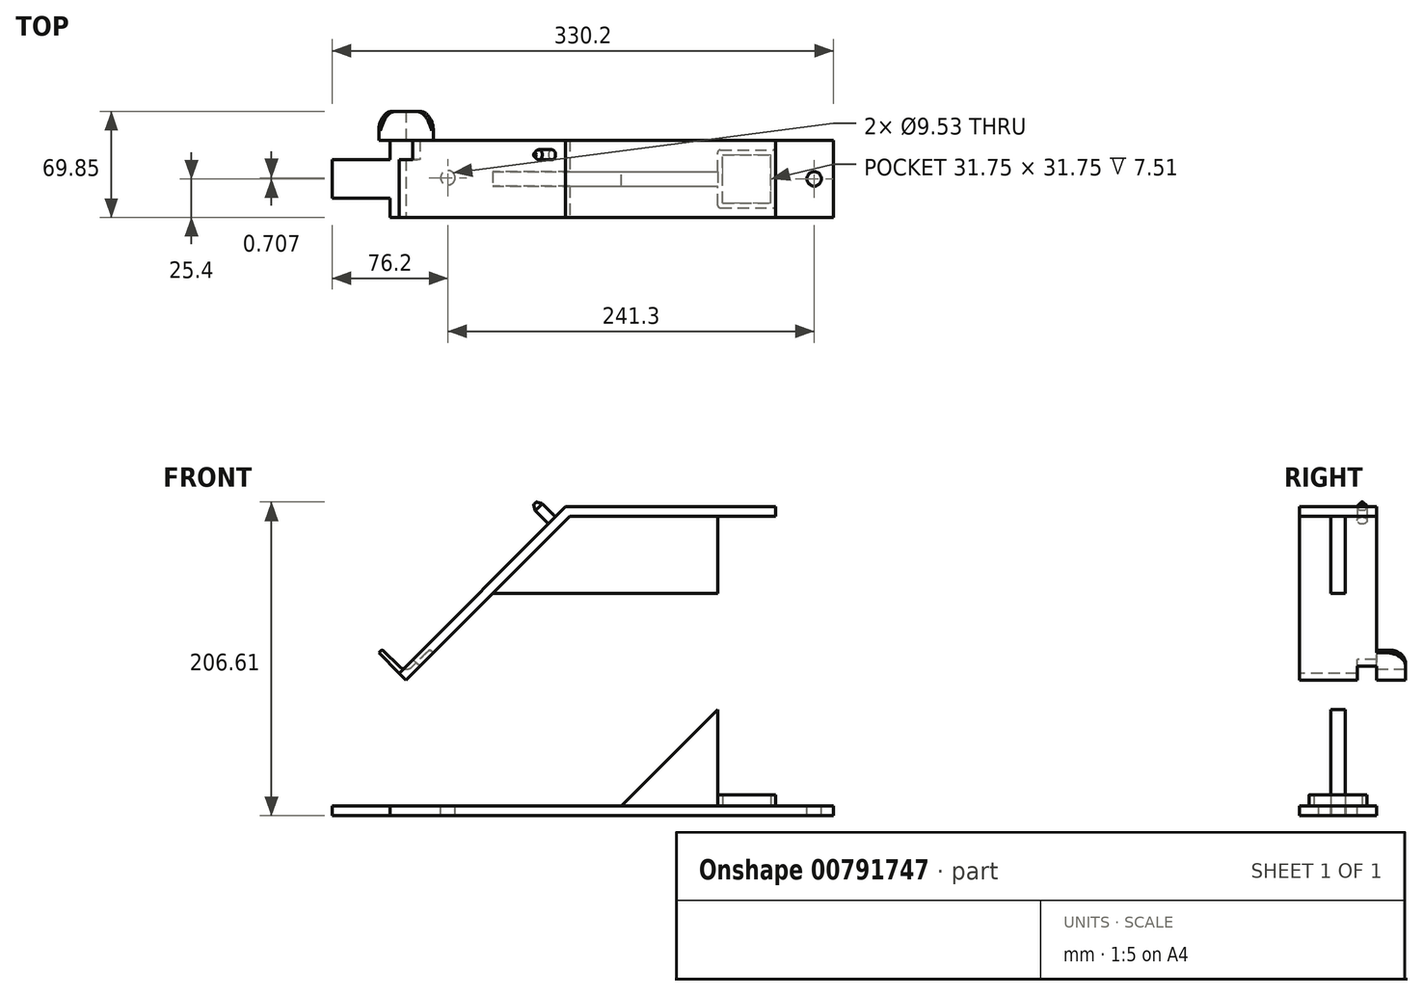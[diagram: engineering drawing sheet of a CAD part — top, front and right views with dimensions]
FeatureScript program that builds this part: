
annotation { "Feature Type Name" : "Feature", "Feature Type Description" : "" }
export const myFeature = defineFeature(function(context is Context, id is Id, definition is map)
    precondition{}
    {
        {
            assignVariable(context, id + "F0", {"name" : "haut", "anyValue" : 8 - 0.49});
        }
        {
            var Q0;
            Q0=qCreatedBy(makeId("Top.planeOp"),FACE);
            var sketch = newSketch(context, id + "F1", { "sketchPlane" : qUnion([Q0])});
            skLineSegment(sketch, "E0.bottom", {"start": v(0, 0) * mm, "end": v(114.3, 0) * mm});
            skLineSegment(sketch, "E0.top", {"start": v(0, 50.8) * mm, "end": v(114.3, 50.8) * mm});
            skLineSegment(sketch, "E0.left", {"start": v(0, 0) * mm, "end": v(0, 50.8) * mm});
            skLineSegment(sketch, "E0.right", {"start": v(114.3, 0) * mm, "end": v(114.3, 50.8) * mm});
            skLineSegment(sketch, "E1.bottom", {"start": v(0, 0) * mm, "end": v(-177.8, 0) * mm});
            skLineSegment(sketch, "E1.top", {"start": v(0, 50.8) * mm, "end": v(-177.8, 50.8) * mm});
            skLineSegment(sketch, "E1.right", {"start": v(-215.9, 12.7) * mm, "end": v(-215.9, 38.1) * mm});
            skLineSegment(sketch, "E2.top", {"start": v(-215.9, 38.1) * mm, "end": v(-177.8, 38.1) * mm});
            skLineSegment(sketch, "E2.right", {"start": v(-177.8, 50.8) * mm, "end": v(-177.8, 38.1) * mm});
            skLineSegment(sketch, "E3.top", {"start": v(-215.9, 12.7) * mm, "end": v(-177.8, 12.7) * mm});
            skLineSegment(sketch, "E3.right", {"start": v(-177.8, 0) * mm, "end": v(-177.8, 12.7) * mm});
            skCircle(sketch, "E4", {"center": v(101.6, 25.4) * mm, "radius": 4.76 * mm});
            skCircle(sketch, "E5", {"center": v(-139.7, 26.1) * mm, "radius": 4.76 * mm});
            skSolve(sketch);
        }
        {
            var Q0;
            Q0=qSketchRegion(id+"F1",true);
            extrude(context, id + "F2", {"entities" : qUnion([Q0]), "oppositeDirection" : true, "depth" : 6.35 * mm, "offsetDistance" : 25.4 * mm});
        }
        {
            var Q0;
            Q0=makeQuery(id+"F2.opExtrude","CAP_FACE",FACE,{"disambiguationData":[OSD([sQuery(id+"F1.wireOp",EDGE,"E0.bottom"),sQuery(id+"F1.wireOp",EDGE,"E0.top"),sQuery(id+"F1.wireOp",EDGE,"E0.left"),sQuery(id+"F1.wireOp",EDGE,"E0.right")])],"isStart":true});
            var sketch = newSketch(context, id + "F3", { "sketchPlane" : qUnion([Q0])});
            skLineSegment(sketch, "E6.bottom", {"start": v(38.1, 6.35) * mm, "end": v(76.2, 6.35) * mm});
            skLineSegment(sketch, "E6.top", {"start": v(38.1, 44.45) * mm, "end": v(76.2, 44.45) * mm});
            skLineSegment(sketch, "E6.left", {"start": v(38.1, 6.35) * mm, "end": v(38.1, 44.45) * mm});
            skLineSegment(sketch, "E6.right", {"start": v(76.2, 6.35) * mm, "end": v(76.2, 44.45) * mm});
            skLineSegment(sketch, "E7.0", {"start": v(41.27, 41.28) * mm, "end": v(73.03, 41.28) * mm});
            skLineSegment(sketch, "E7.1", {"start": v(41.27, 9.52) * mm, "end": v(41.27, 41.28) * mm});
            skLineSegment(sketch, "E7.2", {"start": v(41.27, 9.52) * mm, "end": v(73.03, 9.53) * mm});
            skLineSegment(sketch, "E7.3", {"start": v(73.03, 9.53) * mm, "end": v(73.03, 41.28) * mm});
            skSolve(sketch);
        }
        {
            var Q0;
            Q0=qSketchRegion(id+"F3",true);
            extrude(context, id + "F4", {"entities" : qUnion([Q0]), "operationType" : NewBodyOperationType.ADD, "depth" : (getVariable(context, 'haut')) * mm, "offsetDistance" : 25.4 * mm});
        }
        {
            var Q0;
            Q0=makeQuery(id+"F4.opExtrude","SWEPT_FACE",FACE,{"disambiguationData":[OSD([sQuery(id+"F3.wireOp",EDGE,"E6.bottom")])]});
            var sketch = newSketch(context, id + "F5", { "sketchPlane" : qUnion([Q0])});
            skLineSegment(sketch, "E8", {"start": v(76.2, 190.76) * mm, "end": v(-59.52, 190.76) * mm});
            skLineSegment(sketch, "E9", {"start": v(-59.52, 190.76) * mm, "end": v(-167.28, 83) * mm});
            skLineSegment(sketch, "E10.0", {"start": v(76.2, 197.11) * mm, "end": v(-62.15, 197.11) * mm});
            skLineSegment(sketch, "E11.0", {"start": v(-62.15, 197.11) * mm, "end": v(-171.77, 87.5) * mm});
            skLineSegment(sketch, "E12", {"start": v(-167.28, 83) * mm, "end": v(-171.77, 87.5) * mm});
            skLineSegment(sketch, "E13", {"start": v(76.2, 190.76) * mm, "end": v(76.2, 197.11) * mm});
            skSolve(sketch);
        }
        {
            var Q0;
            Q0=qSketchRegion(id+"F5",true);
            extrude(context, id + "F6", {"entities" : qUnion([Q0]), "operationType" : NewBodyOperationType.ADD, "oppositeDirection" : true, "depth" : 44.45 * mm, "offsetDistance" : 25.4 * mm, "hasSecondDirection" : true, "secondDirectionOppositeDirection" : false, "secondDirectionDepth" : 6.35 * mm});
        }
        {
            var Q0;
            Q0=makeQuery(id+"F6.opExtrude","SWEPT_FACE",FACE,{"disambiguationData":[OSD([sQuery(id+"F5.wireOp",EDGE,"E11.0")])]});
            var sketch = newSketch(context, id + "F7", { "sketchPlane" : qUnion([Q0])});
            skCircle(sketch, "E14", {"center": v(-41.28, 82.74) * mm, "radius": 3.3 * mm});
            skLineSegment(sketch, "E15.direction1", {"start": v(-41.28, 82.74) * mm, "end": v(-15.88, 82.74) * mm, "construction": true});
            skLineSegment(sketch, "E15.direction2", {"start": v(-41.28, 82.74) * mm, "end": v(-41.28, -44.26) * mm, "construction": true});
            skSolve(sketch);
        }
        {
            var Q0;
            Q0=qSketchRegion(id+"F7",true);
            extrude(context, id + "F8", {"entities" : qUnion([Q0]), "operationType" : NewBodyOperationType.ADD, "depth" : 15.88 * mm, "offsetDistance" : 25.4 * mm});
        }
        {
            var Q0;
            Q0=makeQuery(id+"F8.opExtrude","CAP_EDGE",EDGE,{"disambiguationData":[OSD([sQuery(id+"F7.wireOp",EDGE,"E14")])],"isStart":false});
            var Q1;
            Q1=makeQuery(id+"F8.opExtrude","CAP_EDGE",EDGE,{"disambiguationData":[OSD([sQuery(id+"F7.wireOp",EDGE,"E15.0.1.0")])],"isStart":false});
            chamfer(context, id + "F9", {"entities" : qUnion([Q0, Q1]), "chamferType" : ChamferType.OFFSET_ANGLE, "width" : 2.03 * mm, "oppositeDirection" : false, "angle" : 60 * degree, "tangentPropagation" : true});
        }
        {
            var Q0;
            Q0=makeQuery(id+"F7.imprint","IMPRINT",FACE,{"disambiguationData":[TD([[makeQuery(id+"F7.imprint","IMPRINT",EDGE,{"derivedFrom":sQuery(id+"F7.wireOp",EDGE,"E14")}),-1.0]])]});
            var sketch = newSketch(context, id + "F10", { "sketchPlane" : qUnion([Q0])});
            skLineSegment(sketch, "E16.bottom", {"start": v(-50.8, -59.6) * mm, "end": v(-38.1, -59.6) * mm});
            skLineSegment(sketch, "E16.top", {"start": v(-50.8, -46.9) * mm, "end": v(-38.1, -46.9) * mm});
            skLineSegment(sketch, "E16.left", {"start": v(-50.8, -59.6) * mm, "end": v(-50.8, -46.9) * mm});
            skLineSegment(sketch, "E16.right", {"start": v(-38.1, -59.6) * mm, "end": v(-38.1, -46.9) * mm});
            skSolve(sketch);
        }
        {
            var Q0;
            Q0=qSketchRegion(id+"F10",true);
            extrude(context, id + "F11", {"entities" : qUnion([Q0]), "operationType" : NewBodyOperationType.REMOVE, "oppositeDirection" : true, "depth" : 25.4 * mm, "offsetDistance" : 25.4 * mm});
        }
        {
            var Q0;
            Q0=makeQuery(id+"F6.opExtrude","CAP_FACE",FACE,{"disambiguationData":[OSD([sQuery(id+"F5.wireOp",EDGE,"E8"),sQuery(id+"F5.wireOp",EDGE,"E9"),sQuery(id+"F5.wireOp",EDGE,"E10.0"),sQuery(id+"F5.wireOp",EDGE,"E11.0"),sQuery(id+"F5.wireOp",EDGE,"E12"),sQuery(id+"F5.wireOp",EDGE,"E13")])],"isStart":false});
            var sketch = newSketch(context, id + "F12", { "sketchPlane" : qUnion([Q0])});
            skLineSegment(sketch, "E17", {"start": v(149.32, 100.96) * mm, "end": v(167.28, 83) * mm});
            skLineSegment(sketch, "E18", {"start": v(149.32, 100.96) * mm, "end": v(151.56, 103.2) * mm});
            skLineSegment(sketch, "E19", {"start": v(167.28, 83) * mm, "end": v(185.24, 100.96) * mm});
            skLineSegment(sketch, "E20.0", {"start": v(151.56, 103.2) * mm, "end": v(167.28, 87.5) * mm});
            skLineSegment(sketch, "E21.0", {"start": v(167.28, 87.5) * mm, "end": v(183, 103.2) * mm});
            skLineSegment(sketch, "E22.0", {"start": v(183, 103.2) * mm, "end": v(185.24, 100.96) * mm});
            skSolve(sketch);
        }
        {
            var Q0;
            Q0=qSketchRegion(id+"F12",true);
            extrude(context, id + "F13", {"entities" : qUnion([Q0]), "operationType" : NewBodyOperationType.ADD, "depth" : 19.05 * mm, "offsetDistance" : 25.4 * mm});
        }
        {
            var Q0;
            Q0=makeQuery(id+"F13.opExtrude","CAP_EDGE",EDGE,{"disambiguationData":[OSD([sQuery(id+"F12.wireOp",EDGE,"E22.0")])],"isStart":false});
            fillet(context, id + "F14", {"entities" : qUnion([Q0]), "radius" : 12.7 * mm, "tangentPropagation" : true, "allowEdgeOverflow" : false});
        }
        {
            var Q0;
            Q0=makeQuery(id+"F13.opExtrude","CAP_EDGE",EDGE,{"disambiguationData":[OSD([sQuery(id+"F12.wireOp",EDGE,"E18")])],"isStart":false});
            fillet(context, id + "F15", {"entities" : qUnion([Q0]), "radius" : 12.7 * mm, "tangentPropagation" : true, "allowEdgeOverflow" : false});
        }
        {
            var Q0;
            Q0=makeQuery(id+"F13.opExtrude","SWEPT_EDGE",EDGE,{"disambiguationData":[OSD([sQuery(id+"F12.wireOp",EDGE,"E20.0"),sQuery(id+"F12.wireOp",EDGE,"E21.0")])]});
            fillet(context, id + "F16", {"entities" : qUnion([Q0]), "radius" : 6.35 * mm, "tangentPropagation" : true, "allowEdgeOverflow" : false});
        }
        {
            var Q0;
            Q0=makeQuery(id+"F13.opExtrude","SWEPT_EDGE",EDGE,{"disambiguationData":[OSD([sQuery(id+"F12.wireOp",EDGE,"E21.0"),sQuery(id+"F12.wireOp",EDGE,"E22.0")])]});
            var Q1;
            Q1=makeQuery(id+"F13.opExtrude","SWEPT_EDGE",EDGE,{"disambiguationData":[OSD([sQuery(id+"F12.wireOp",EDGE,"E18"),sQuery(id+"F12.wireOp",EDGE,"E20.0")])]});
            fillet(context, id + "F17", {"entities" : qUnion([Q0, Q1]), "radius" : 1.59 * mm, "allowEdgeOverflow" : false});
        }
        {
            var Q0;
            Q0=makeQuery(id+"F4.opExtrude","SWEPT_FACE",FACE,{"disambiguationData":[OSD([sQuery(id+"F3.wireOp",EDGE,"E6.left")])]});
            var sketch = newSketch(context, id + "F18", { "sketchPlane" : qUnion([Q0])});
            skLineSegment(sketch, "E23.bottom", {"start": v(-30.16, 190.76) * mm, "end": v(-20.64, 190.76) * mm});
            skLineSegment(sketch, "E23.top", {"start": v(-30.16, 139.96) * mm, "end": v(-20.64, 139.96) * mm});
            skLineSegment(sketch, "E23.left", {"start": v(-30.16, 190.76) * mm, "end": v(-30.16, 139.96) * mm});
            skLineSegment(sketch, "E23.right", {"start": v(-20.64, 190.76) * mm, "end": v(-20.64, 139.96) * mm});
            skSolve(sketch);
        }
        {
            var Q0;
            Q0=qSketchRegion(id+"F18",true);
            extrude(context, id + "F19", {"entities" : qUnion([Q0]), "operationType" : NewBodyOperationType.ADD, "endBound" : BoundingType.UP_TO_NEXT, "depth" : 25.4 * mm, "offsetDistance" : 25.4 * mm});
        }
        {
            var Q0;
            Q0=makeQuery(id+"F4.opExtrude","SWEPT_EDGE",EDGE,{"disambiguationData":[OSD([sQuery(id+"F3.wireOp",EDGE,"E6.bottom"),sQuery(id+"F3.wireOp",EDGE,"E6.right")])]});
            var Q1;
            Q1=makeQuery(id+"F4.opExtrude","SWEPT_EDGE",EDGE,{"disambiguationData":[OSD([sQuery(id+"F3.wireOp",EDGE,"E6.bottom"),sQuery(id+"F3.wireOp",EDGE,"E6.left")])]});
            var Q2;
            Q2=makeQuery(id+"F4.opExtrude","SWEPT_EDGE",EDGE,{"disambiguationData":[OSD([sQuery(id+"F3.wireOp",EDGE,"E6.top"),sQuery(id+"F3.wireOp",EDGE,"E6.right")])]});
            var Q3;
            Q3=makeQuery(id+"F4.opExtrude","SWEPT_EDGE",EDGE,{"disambiguationData":[OSD([sQuery(id+"F3.wireOp",EDGE,"E6.top"),sQuery(id+"F3.wireOp",EDGE,"E6.left")])]});
            fillet(context, id + "F20", {"entities" : qUnion([Q0, Q1, Q2, Q3]), "radius" : 1.59 * mm, "tangentPropagation" : true, "allowEdgeOverflow" : false});
        }
        {
            var Q0;
            Q0=qCreatedBy(makeId("Front.planeOp"),FACE);
            cPlane(context, id + "F21", {"entities" : qUnion([Q0]), "cplaneType" : CPlaneType.OFFSET, "offset" : 25.4 * mm, "oppositeDirection" : true, "width" : 152.4 * mm, "height" : 152.4 * mm});
        }
        {
            var Q0;
            Q0=qCreatedBy(id+"F21.planeOp",FACE);
            var sketch = newSketch(context, id + "F22", { "sketchPlane" : qUnion([Q0])});
            skLineSegment(sketch, "E24", {"start": v(38.1, 63.5) * mm, "end": v(-25.4, 0) * mm});
            skLineSegment(sketch, "E25", {"start": v(38.1, 63.5) * mm, "end": v(38.1, 0) * mm});
            skLineSegment(sketch, "E26", {"start": v(-25.4, 0) * mm, "end": v(38.1, 0) * mm});
            skSolve(sketch);
        }
        {
            var Q0;
            Q0=qSketchRegion(id+"F22",true);
            extrude(context, id + "F23", {"entities" : qUnion([Q0]), "operationType" : NewBodyOperationType.ADD, "depth" : 4.76 * mm, "offsetDistance" : 25.4 * mm, "hasSecondDirection" : true, "secondDirectionOppositeDirection" : true, "secondDirectionDepth" : 4.76 * mm});
        }
    });
